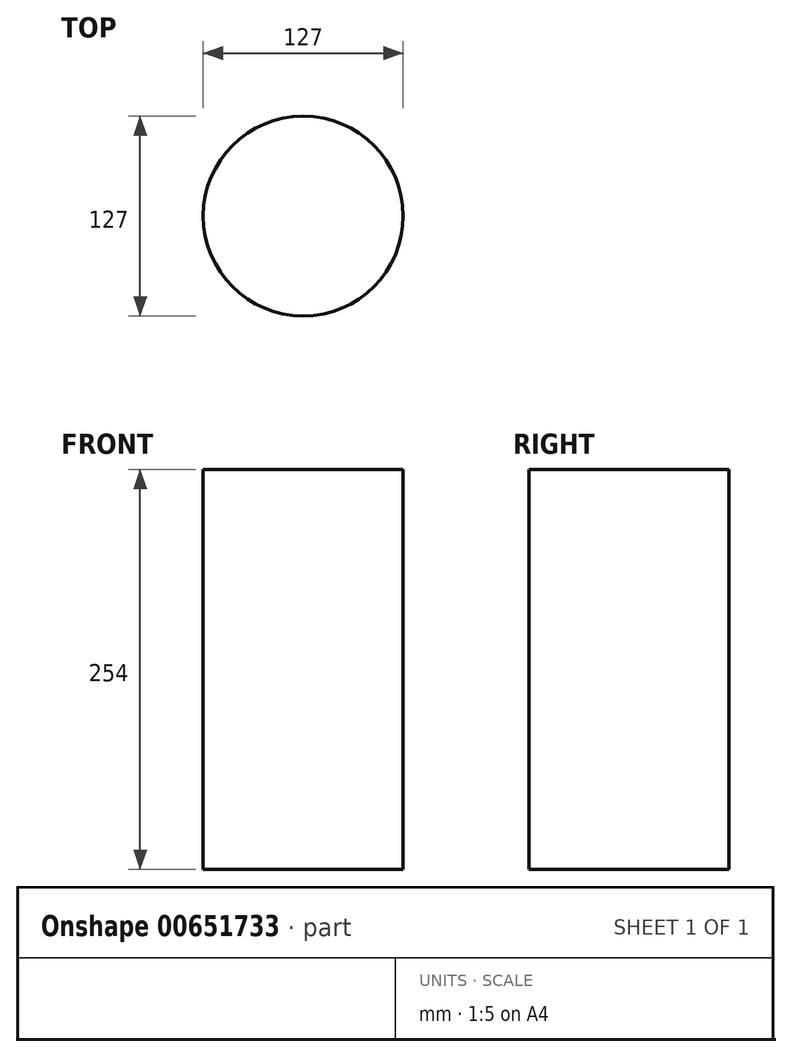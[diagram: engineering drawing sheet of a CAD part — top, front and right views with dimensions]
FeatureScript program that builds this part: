
annotation { "Feature Type Name" : "Feature", "Feature Type Description" : "" }
export const myFeature = defineFeature(function(context is Context, id is Id, definition is map)
    precondition{}
    {
        {
            var Q0;
            Q0=qCreatedBy(makeId("Top.planeOp"),FACE);
            var sketch = newSketch(context, id + "F0", { "sketchPlane" : qUnion([Q0])});
            skCircle(sketch, "E0", {"center": v(0, 0) * mm, "radius": 63.5 * mm});
            skSolve(sketch);
        }
        {
            var Q0;
            Q0 = qSketchRegion(id + "F0", true);
            extrude(context, id + "F1", {"entities" : qUnion([Q0]), "depth" : 254 * mm, "offsetDistance" : 25.4 * mm});
        }
        {
            var Q0;
            Q0=makeQuery(id+"F1.opExtrude","CAP_FACE",FACE,{"disambiguationData":[OSD([sQuery(id+"F0.wireOp",EDGE,"E0")])],"isStart":false});
            var sketch = newSketch(context, id + "F2", { "sketchPlane" : qUnion([Q0])});
            skLineSegment(sketch, "E1", {"start": v(0, 0) * mm, "end": v(56.92, 28.16) * mm});
            skSolve(sketch);
        }
    });
